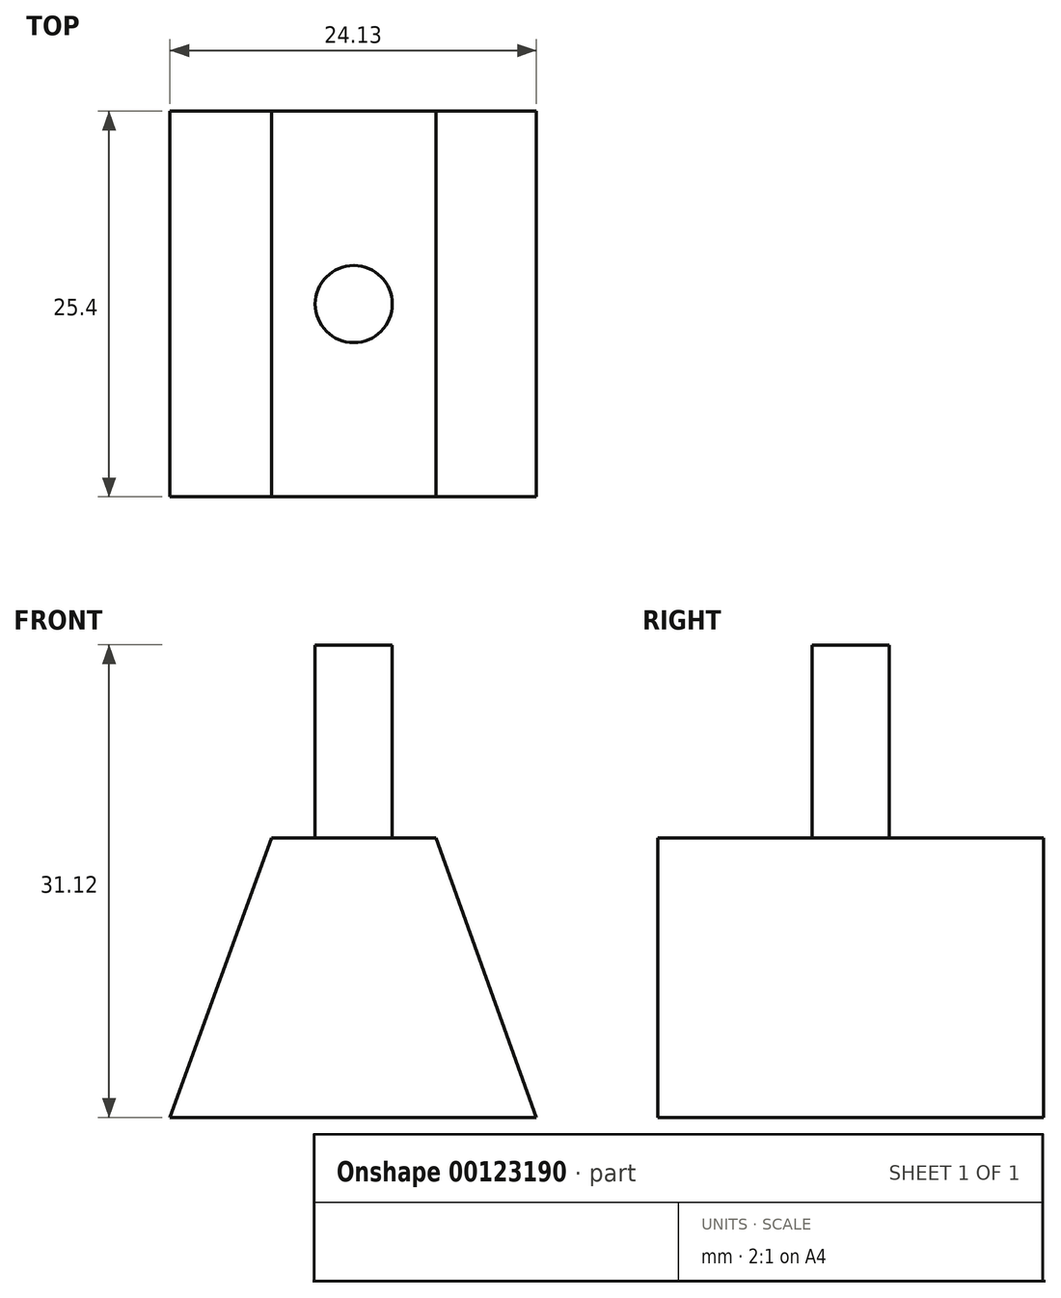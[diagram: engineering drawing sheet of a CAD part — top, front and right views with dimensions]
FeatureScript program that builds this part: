
annotation { "Feature Type Name" : "Feature", "Feature Type Description" : "" }
export const myFeature = defineFeature(function(context is Context, id is Id, definition is map)
    precondition{}
    {
        {
            var Q0;
            Q0=qCreatedBy(makeId("Front.planeOp"),FACE);
            var sketch = newSketch(context, id + "F0", { "sketchPlane" : qUnion([Q0])});
            skLineSegment(sketch, "E0", {"start": v(-12.07, 0) * mm, "end": v(12.07, 0) * mm});
            skLineSegment(sketch, "E1", {"start": v(12.07, 0) * mm, "end": v(5.43, 18.41) * mm});
            skLineSegment(sketch, "E2", {"start": v(-12.07, 0) * mm, "end": v(-5.36, 18.41) * mm});
            skLineSegment(sketch, "E3", {"start": v(-5.36, 18.41) * mm, "end": v(5.43, 18.41) * mm});
            skSolve(sketch);
        }
        {
            var Q0;
            Q0 = qSketchRegion(id + "F0", true);
            extrude(context, id + "F1", {"entities" : qUnion([Q0]), "oppositeDirection" : true, "depth" : 25.4 * mm});
        }
        {
            var Q0;
            Q0=makeQuery(id+"F1.opExtrude","SWEPT_FACE",FACE,{"disambiguationData":[OSD([sQuery(id+"F0.wireOp",EDGE,"E3")])]});
            var sketch = newSketch(context, id + "F2", { "sketchPlane" : qUnion([Q0])});
            skCircle(sketch, "E4", {"center": v(0.04, 12.7) * mm, "radius": 2.54 * mm});
            skPoint(sketch, "E4.centerSnap0", {"position": v(-5.36, 12.7) * mm});
            skPoint(sketch, "E4.centerSnap1", {"position": v(0.04, 25.4) * mm});
            skSolve(sketch);
        }
        {
            var Q0;
            Q0 = qSketchRegion(id + "F2", true);
            extrude(context, id + "F3", {"entities" : qUnion([Q0]), "operationType" : NewBodyOperationType.ADD, "depth" : 12.7 * mm});
        }
    });
